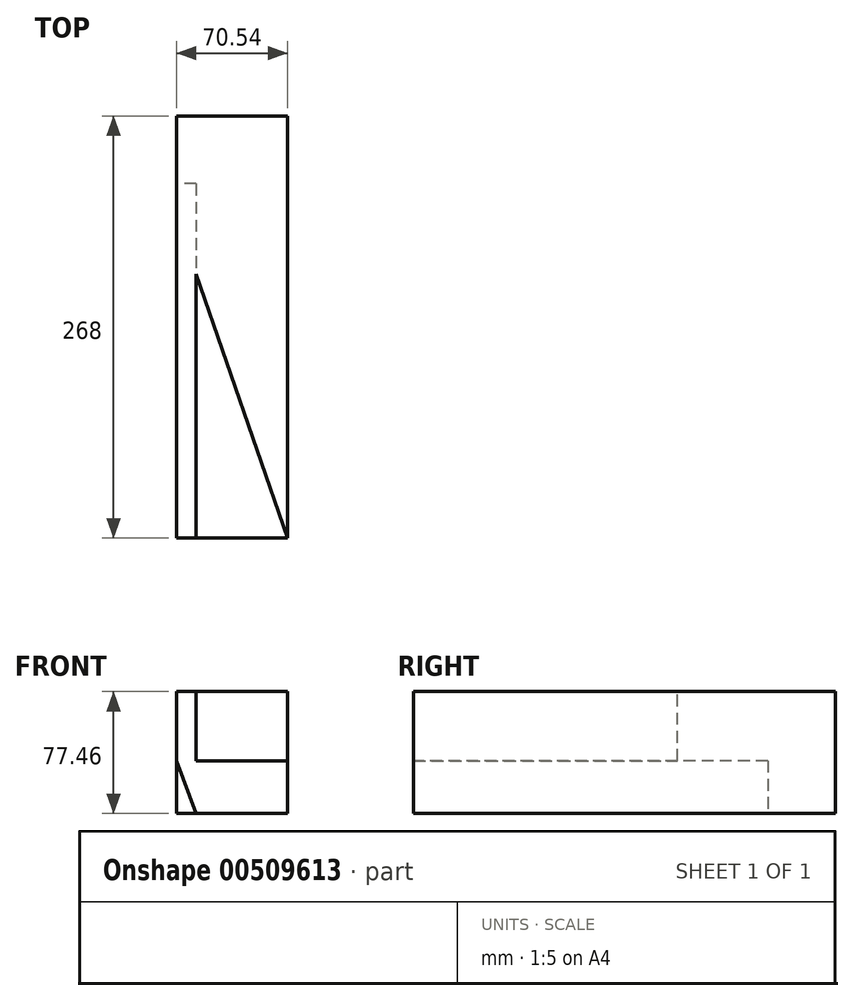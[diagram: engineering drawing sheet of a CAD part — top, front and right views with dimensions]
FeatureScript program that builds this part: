
annotation { "Feature Type Name" : "Feature", "Feature Type Description" : "" }
export const myFeature = defineFeature(function(context is Context, id is Id, definition is map)
    precondition{}
    {
        {
            var Q0;
            Q0=qCreatedBy(makeId("Front.planeOp"),FACE);
            var sketch = newSketch(context, id + "F0", { "sketchPlane" : qUnion([Q0])});
            skLineSegment(sketch, "E0.bottom", {"start": v(35.27, 38.73) * mm, "end": v(-35.27, 38.73) * mm});
            skLineSegment(sketch, "E0.top", {"start": v(35.27, -38.73) * mm, "end": v(-35.27, -38.73) * mm});
            skLineSegment(sketch, "E0.left", {"start": v(35.27, 38.73) * mm, "end": v(35.27, -38.73) * mm});
            skLineSegment(sketch, "E0.right", {"start": v(-35.27, 38.73) * mm, "end": v(-35.27, -38.73) * mm});
            skPoint(sketch, "E0.middle", {"position": v(0, 0) * mm});
            skSolve(sketch);
        }
        {
            var Q0;
            Q0=makeQuery(id+"F0.imprint","IMPRINT",FACE,{"disambiguationData":[TD([[makeQuery(id+"F0.imprint","IMPRINT",EDGE,{"derivedFrom":sQuery(id+"F0.wireOp",EDGE,"E0.bottom")}),1.0]])]});
            extrude(context, id + "F1", {"entities" : qUnion([Q0]), "endBound" : BoundingType.SYMMETRIC, "depth" : 268 * mm});
        }
        {
            var Q0;
            Q0=makeQuery(id+"F1.opExtrude","SWEPT_FACE",FACE,{"disambiguationData":[OSD([sQuery(id+"F0.wireOp",EDGE,"E0.bottom")])]});
            var sketch = newSketch(context, id + "F2", { "sketchPlane" : qUnion([Q0])});
            skLineSegment(sketch, "E1", {"start": v(-22.86, -134) * mm, "end": v(-22.86, 33.64) * mm});
            skLineSegment(sketch, "E2", {"start": v(-22.86, 33.64) * mm, "end": v(35.27, -134) * mm});
            skLineSegment(sketch, "E3", {"start": v(35.27, -134) * mm, "end": v(-22.86, -134) * mm});
            skSolve(sketch);
        }
        {
            var Q0;
            Q0=makeQuery(id+"F2.imprint","IMPRINT",FACE,{"disambiguationData":[TD([[makeQuery(id+"F2.imprint","IMPRINT",EDGE,{"derivedFrom":sQuery(id+"F2.wireOp",EDGE,"E1")}),-1.0]])]});
            extrude(context, id + "F3", {"entities" : qUnion([Q0]), "operationType" : NewBodyOperationType.REMOVE, "oppositeDirection" : true, "depth" : 44 * mm});
        }
        {
            var Q0;
            Q0=makeQuery(id+"F1.opExtrude","CAP_FACE",FACE,{"disambiguationData":[OSD([sQuery(id+"F0.wireOp",EDGE,"E0.bottom"),sQuery(id+"F0.wireOp",EDGE,"E0.top"),sQuery(id+"F0.wireOp",EDGE,"E0.left"),sQuery(id+"F0.wireOp",EDGE,"E0.right")])],"isStart":false});
            var sketch = newSketch(context, id + "F4", { "sketchPlane" : qUnion([Q0])});
            skLineSegment(sketch, "E4", {"start": v(-35.27, -5.27) * mm, "end": v(-22.86, -38.73) * mm});
            skLineSegment(sketch, "E5", {"start": v(-22.86, -38.73) * mm, "end": v(-35.27, -38.73) * mm});
            skLineSegment(sketch, "E6", {"start": v(-35.27, -38.73) * mm, "end": v(-35.27, -5.27) * mm});
            skSolve(sketch);
        }
        {
            var Q0;
            Q0=makeQuery(id+"F4.imprint","IMPRINT",FACE,{"disambiguationData":[TD([[makeQuery(id+"F4.imprint","IMPRINT",EDGE,{"derivedFrom":sQuery(id+"F4.wireOp",EDGE,"E4")}),-1.0]])]});
            extrude(context, id + "F5", {"entities" : qUnion([Q0]), "operationType" : NewBodyOperationType.REMOVE, "oppositeDirection" : true, "depth" : 225 * mm});
        }
    });
